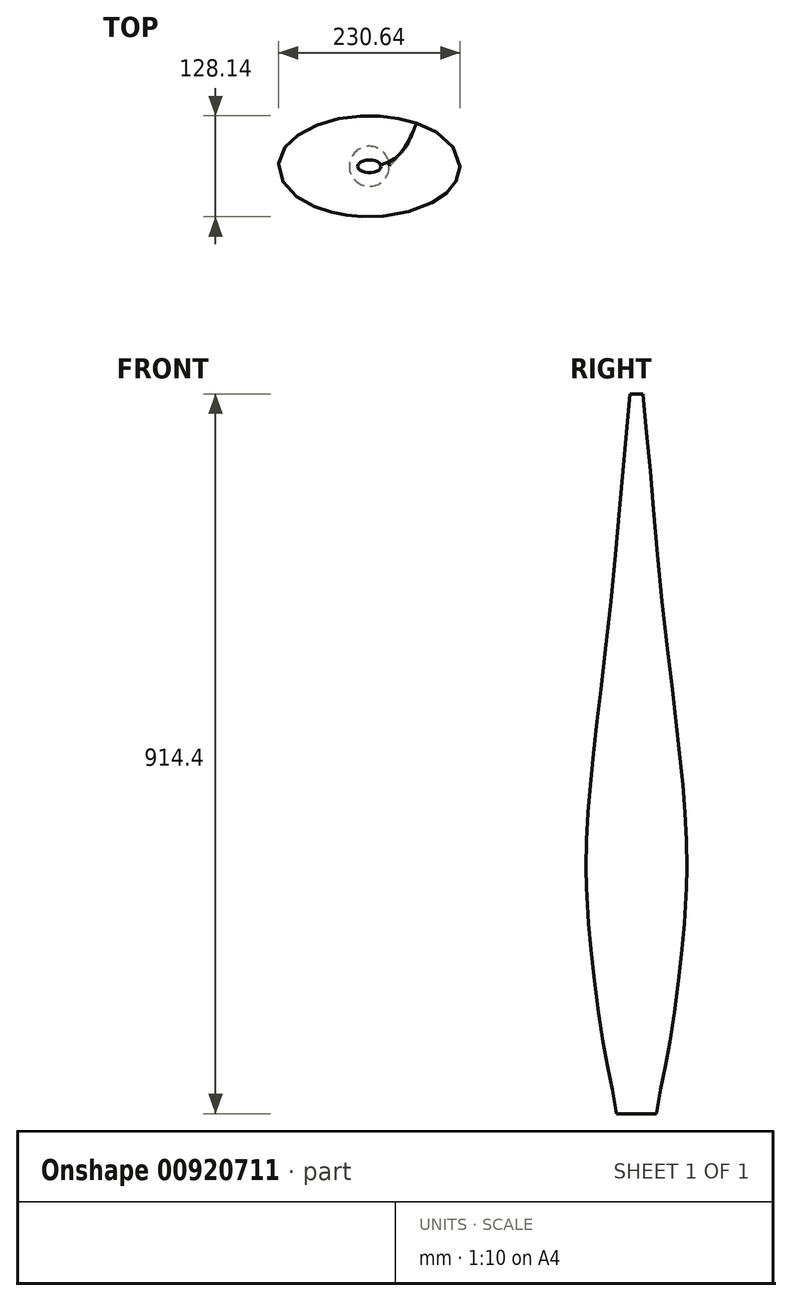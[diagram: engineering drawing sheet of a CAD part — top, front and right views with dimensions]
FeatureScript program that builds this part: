
annotation { "Feature Type Name" : "Feature", "Feature Type Description" : "" }
export const myFeature = defineFeature(function(context is Context, id is Id, definition is map)
    precondition{}
    {
        {
            var Q0;
            Q0=qCreatedBy(makeId("Top.planeOp"),FACE);
            var sketch = newSketch(context, id + "F0", { "sketchPlane" : qUnion([Q0])});
            skEllipse(sketch, "E0", {"center": v(0, 0) * mm, "majorRadius": 25.4 * mm, "minorRadius": 25.4 * mm, "majorAxis": v(1, 0)});
            skSolve(sketch);
        }
        {
            var Q0;
            Q0=qCreatedBy(makeId("Front.planeOp"),FACE);
            var sketch = newSketch(context, id + "F1", { "sketchPlane" : qUnion([Q0])});
            skLineSegment(sketch, "E1", {"start": v(0, 0) * mm, "end": v(0, 101.6) * mm, "construction": true});
            skPoint(sketch, "E2", {"position": v(0, 101.6) * mm});
            skPoint(sketch, "E3.0.1.0", {"position": v(0, 203.2) * mm});
            skPoint(sketch, "E3.0.2.0", {"position": v(0, 304.8) * mm});
            skPoint(sketch, "E3.0.3.0", {"position": v(0, 406.4) * mm});
            skPoint(sketch, "E3.0.4.0", {"position": v(0, 508) * mm});
            skPoint(sketch, "E3.0.5.0", {"position": v(0, 609.6) * mm});
            skPoint(sketch, "E3.0.6.0", {"position": v(0, 711.2) * mm});
            skPoint(sketch, "E3.0.7.0", {"position": v(0, 812.8) * mm});
            skPoint(sketch, "E3.0.8.0", {"position": v(0, 914.4) * mm});
            skLineSegment(sketch, "E3.direction1", {"start": v(0, 101.6) * mm, "end": v(25.4, 101.6) * mm, "construction": true});
            skLineSegment(sketch, "E3.direction2", {"start": v(0, 101.6) * mm, "end": v(0, 203.2) * mm, "construction": true});
            skSolve(sketch);
        }
        {
            var Q0;
            Q0=qCreatedBy(makeId("Top.planeOp"),FACE);
            var Q1;
            Q1=sQuery(id+"F1.wireOp",VERTEX,"E2");
            cPlane(context, id + "F2", {"entities" : qUnion([Q0, Q1]), "cplaneType" : CPlaneType.PLANE_POINT, "offset" : 25.4 * mm, "width" : 152.4 * mm, "height" : 152.4 * mm});
        }
        {
            var Q0;
            Q0=qCreatedBy(makeId("Top.planeOp"),FACE);
            var Q1;
            Q1=sQuery(id+"F1.wireOp",VERTEX,"E3.0.1.0");
            cPlane(context, id + "F3", {"entities" : qUnion([Q0, Q1]), "cplaneType" : CPlaneType.PLANE_POINT, "offset" : 25.4 * mm, "width" : 152.4 * mm, "height" : 152.4 * mm});
        }
        {
            var Q0;
            Q0=qCreatedBy(makeId("Top.planeOp"),FACE);
            var Q1;
            Q1=sQuery(id+"F1.wireOp",VERTEX,"E3.0.2.0");
            cPlane(context, id + "F4", {"entities" : qUnion([Q0, Q1]), "cplaneType" : CPlaneType.PLANE_POINT, "offset" : 25.4 * mm, "width" : 152.4 * mm, "height" : 152.4 * mm});
        }
        {
            var Q0;
            Q0=qCreatedBy(makeId("Top.planeOp"),FACE);
            var Q1;
            Q1=sQuery(id+"F1.wireOp",VERTEX,"E3.0.3.0");
            cPlane(context, id + "F5", {"entities" : qUnion([Q0, Q1]), "cplaneType" : CPlaneType.PLANE_POINT, "offset" : 25.4 * mm, "width" : 152.4 * mm, "height" : 152.4 * mm});
        }
        {
            var Q0;
            Q0=qCreatedBy(makeId("Top.planeOp"),FACE);
            var Q1;
            Q1=sQuery(id+"F1.wireOp",VERTEX,"E3.0.4.0");
            cPlane(context, id + "F6", {"entities" : qUnion([Q0, Q1]), "cplaneType" : CPlaneType.PLANE_POINT, "offset" : 25.4 * mm, "width" : 152.4 * mm, "height" : 152.4 * mm});
        }
        {
            var Q0;
            Q0=qCreatedBy(makeId("Top.planeOp"),FACE);
            var Q1;
            Q1=sQuery(id+"F1.wireOp",VERTEX,"E3.0.5.0");
            cPlane(context, id + "F7", {"entities" : qUnion([Q0, Q1]), "cplaneType" : CPlaneType.PLANE_POINT, "offset" : 25.4 * mm, "width" : 152.4 * mm, "height" : 152.4 * mm});
        }
        {
            var Q0;
            Q0=qCreatedBy(makeId("Top.planeOp"),FACE);
            var Q1;
            Q1=sQuery(id+"F1.wireOp",VERTEX,"E3.0.6.0");
            cPlane(context, id + "F8", {"entities" : qUnion([Q0, Q1]), "cplaneType" : CPlaneType.PLANE_POINT, "offset" : 25.4 * mm, "width" : 152.4 * mm, "height" : 152.4 * mm});
        }
        {
            var Q0;
            Q0=qCreatedBy(makeId("Top.planeOp"),FACE);
            var Q1;
            Q1=sQuery(id+"F1.wireOp",VERTEX,"E3.0.7.0");
            cPlane(context, id + "F9", {"entities" : qUnion([Q0, Q1]), "cplaneType" : CPlaneType.PLANE_POINT, "offset" : 25.4 * mm, "width" : 152.4 * mm, "height" : 152.4 * mm});
        }
        {
            var Q0;
            Q0=qCreatedBy(makeId("Top.planeOp"),FACE);
            var Q1;
            Q1=sQuery(id+"F1.wireOp",VERTEX,"E3.0.8.0");
            cPlane(context, id + "F10", {"entities" : qUnion([Q0, Q1]), "cplaneType" : CPlaneType.PLANE_POINT, "offset" : 25.4 * mm, "width" : 152.4 * mm, "height" : 152.4 * mm});
        }
        {
            var Q0;
            Q0=qCreatedBy(id+"F2.planeOp",FACE);
            var sketch = newSketch(context, id + "F11", { "sketchPlane" : qUnion([Q0])});
            skEllipse(sketch, "E4", {"center": v(0, 0) * mm, "majorRadius": 63.5 * mm, "minorRadius": 44.45 * mm, "majorAxis": v(1, 0)});
            skSolve(sketch);
        }
        {
            var Q0;
            Q0=qCreatedBy(id+"F3.planeOp",FACE);
            var sketch = newSketch(context, id + "F12", { "sketchPlane" : qUnion([Q0])});
            skEllipse(sketch, "E5", {"center": v(0, 0) * mm, "majorRadius": 102.74 * mm, "minorRadius": 57.15 * mm, "majorAxis": v(1, 0)});
            skSolve(sketch);
        }
        {
            var Q0;
            Q0=qCreatedBy(id+"F4.planeOp",FACE);
            var sketch = newSketch(context, id + "F13", { "sketchPlane" : qUnion([Q0])});
            skEllipse(sketch, "E6", {"center": v(0, 0) * mm, "majorRadius": 115.32 * mm, "minorRadius": 64 * mm, "majorAxis": v(1, 0)});
            skSolve(sketch);
        }
        {
            var Q0;
            Q0=qCreatedBy(id+"F5.planeOp",FACE);
            var sketch = newSketch(context, id + "F14", { "sketchPlane" : qUnion([Q0])});
            skEllipse(sketch, "E7", {"center": v(0, 0) * mm, "majorRadius": 107.44 * mm, "minorRadius": 59.7 * mm, "majorAxis": v(1, 0)});
            skSolve(sketch);
        }
        {
            var Q0;
            Q0=qCreatedBy(id+"F6.planeOp",FACE);
            var sketch = newSketch(context, id + "F15", { "sketchPlane" : qUnion([Q0])});
            skEllipse(sketch, "E8", {"center": v(0, 0) * mm, "majorRadius": 88.52 * mm, "minorRadius": 49.15 * mm, "majorAxis": v(1, 0)});
            skSolve(sketch);
        }
        {
            var Q0;
            Q0=qCreatedBy(id+"F7.planeOp",FACE);
            var sketch = newSketch(context, id + "F16", { "sketchPlane" : qUnion([Q0])});
            skEllipse(sketch, "E9", {"center": v(0, 0) * mm, "majorRadius": 66.3 * mm, "minorRadius": 36.83 * mm, "majorAxis": v(1, 0)});
            skSolve(sketch);
        }
        {
            var Q0;
            Q0=qCreatedBy(id+"F8.planeOp",FACE);
            var sketch = newSketch(context, id + "F17", { "sketchPlane" : qUnion([Q0])});
            skEllipse(sketch, "E10", {"center": v(0, 0) * mm, "majorRadius": 47.5 * mm, "minorRadius": 26.42 * mm, "majorAxis": v(1, 0)});
            skSolve(sketch);
        }
        {
            var Q0;
            Q0=qCreatedBy(id+"F9.planeOp",FACE);
            var sketch = newSketch(context, id + "F18", { "sketchPlane" : qUnion([Q0])});
            skEllipse(sketch, "E11", {"center": v(0, 0) * mm, "majorRadius": 31.75 * mm, "minorRadius": 17.78 * mm, "majorAxis": v(1, 0)});
            skSolve(sketch);
        }
        {
            var Q0;
            Q0=qCreatedBy(id+"F10.planeOp",FACE);
            var sketch = newSketch(context, id + "F19", { "sketchPlane" : qUnion([Q0])});
            skEllipse(sketch, "E12", {"center": v(0, 0) * mm, "majorRadius": 14.73 * mm, "minorRadius": 8.13 * mm, "majorAxis": v(1, 0)});
            skSolve(sketch);
        }
        {
            var Q0;
            Q0=makeQuery(id+"F0.imprint","IMPRINT",FACE,{"disambiguationData":[TD([[makeQuery(id+"F0.imprint","IMPRINT",EDGE,{"derivedFrom":sQuery(id+"F0.wireOp",EDGE,"E0")}),1.0]])]});
            var Q1;
            Q1=makeQuery(id+"F11.imprint","IMPRINT",FACE,{"disambiguationData":[TD([[makeQuery(id+"F11.imprint","IMPRINT",EDGE,{"derivedFrom":sQuery(id+"F11.wireOp",EDGE,"E4")}),1.0]])]});
            var Q2;
            Q2=makeQuery(id+"F12.imprint","IMPRINT",FACE,{"disambiguationData":[TD([[makeQuery(id+"F12.imprint","IMPRINT",EDGE,{"derivedFrom":sQuery(id+"F12.wireOp",EDGE,"E5")}),1.0]])]});
            var Q3;
            Q3=makeQuery(id+"F13.imprint","IMPRINT",FACE,{"disambiguationData":[TD([[makeQuery(id+"F13.imprint","IMPRINT",EDGE,{"derivedFrom":sQuery(id+"F13.wireOp",EDGE,"E6")}),1.0]])]});
            var Q4;
            Q4=makeQuery(id+"F14.imprint","IMPRINT",FACE,{"disambiguationData":[TD([[makeQuery(id+"F14.imprint","IMPRINT",EDGE,{"derivedFrom":sQuery(id+"F14.wireOp",EDGE,"E7")}),1.0]])]});
            var Q5;
            Q5=makeQuery(id+"F15.imprint","IMPRINT",FACE,{"disambiguationData":[TD([[makeQuery(id+"F15.imprint","IMPRINT",EDGE,{"derivedFrom":sQuery(id+"F15.wireOp",EDGE,"E8")}),1.0]])]});
            var Q6;
            Q6=makeQuery(id+"F16.imprint","IMPRINT",FACE,{"disambiguationData":[TD([[makeQuery(id+"F16.imprint","IMPRINT",EDGE,{"derivedFrom":sQuery(id+"F16.wireOp",EDGE,"E9")}),1.0]])]});
            var Q7;
            Q7=makeQuery(id+"F17.imprint","IMPRINT",FACE,{"disambiguationData":[TD([[makeQuery(id+"F17.imprint","IMPRINT",EDGE,{"derivedFrom":sQuery(id+"F17.wireOp",EDGE,"E10")}),1.0]])]});
            var Q8;
            Q8=makeQuery(id+"F18.imprint","IMPRINT",FACE,{"disambiguationData":[TD([[makeQuery(id+"F18.imprint","IMPRINT",EDGE,{"derivedFrom":sQuery(id+"F18.wireOp",EDGE,"E11")}),1.0]])]});
            var Q9;
            Q9=makeQuery(id+"F19.imprint","IMPRINT",FACE,{"disambiguationData":[TD([[makeQuery(id+"F19.imprint","IMPRINT",EDGE,{"derivedFrom":sQuery(id+"F19.wireOp",EDGE,"E12")}),1.0]])]});
            loft(context, id + "F20", {"sheetProfilesArray" : [{ "sheetProfileEntities" : qUnion([Q0]) }, { "sheetProfileEntities" : qUnion([Q1]) }, { "sheetProfileEntities" : qUnion([Q2]) }, { "sheetProfileEntities" : qUnion([Q3]) }, { "sheetProfileEntities" : qUnion([Q4]) }, { "sheetProfileEntities" : qUnion([Q5]) }, { "sheetProfileEntities" : qUnion([Q6]) }, { "sheetProfileEntities" : qUnion([Q7]) }, { "sheetProfileEntities" : qUnion([Q8]) }, { "sheetProfileEntities" : qUnion([Q9]) }]});
        }
    });
